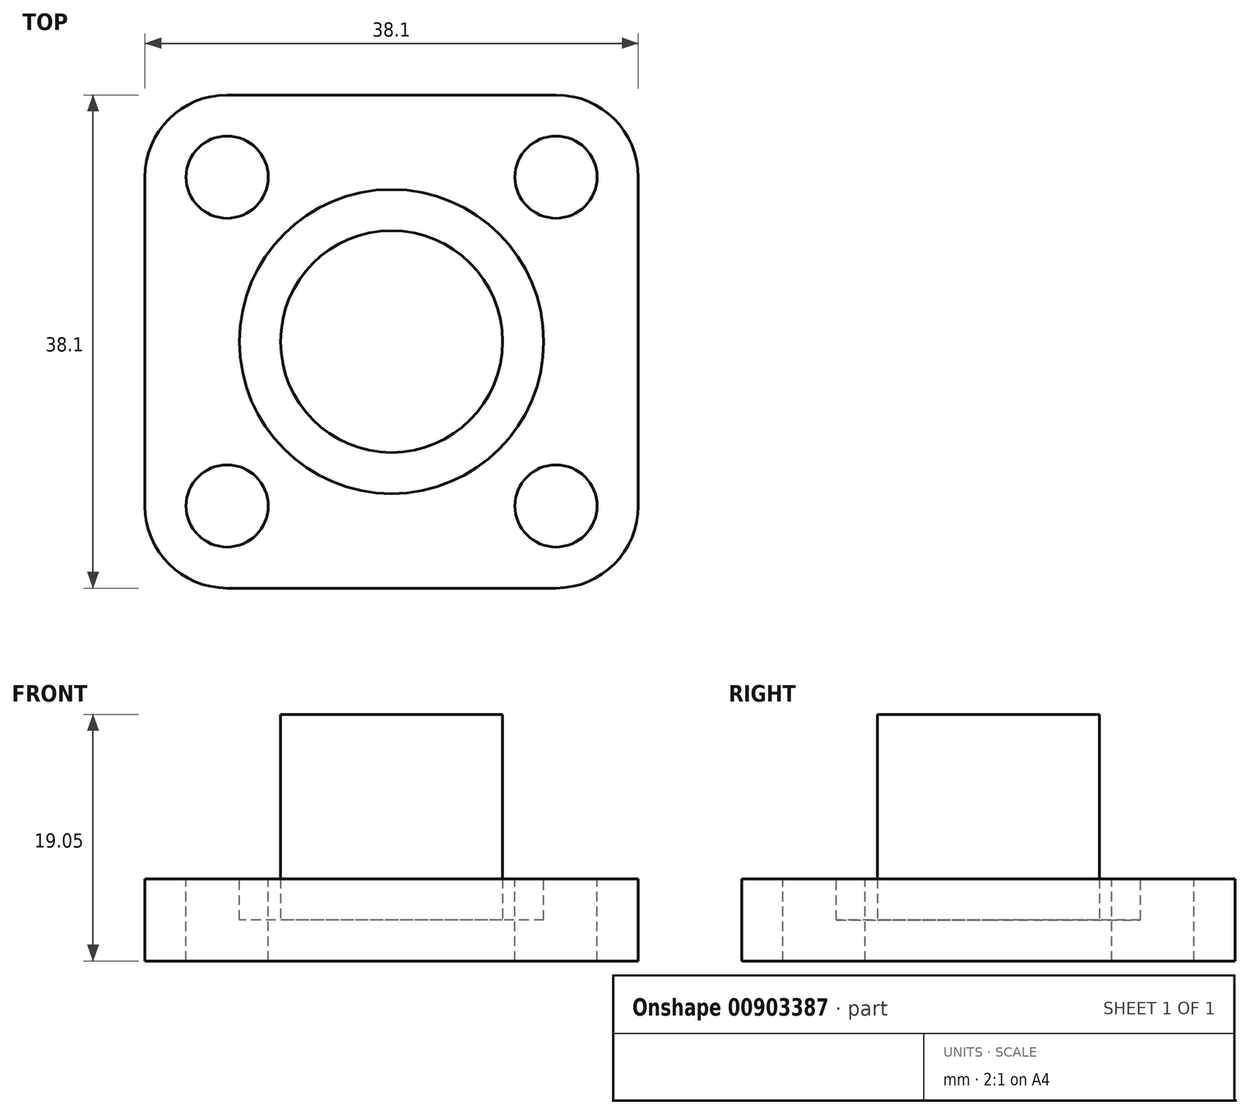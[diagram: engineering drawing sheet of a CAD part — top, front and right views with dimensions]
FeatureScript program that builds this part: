
annotation { "Feature Type Name" : "Feature", "Feature Type Description" : "" }
export const myFeature = defineFeature(function(context is Context, id is Id, definition is map)
    precondition{}
    {
        {
            var Q0;
            Q0=qCreatedBy(makeId("Top.planeOp"),FACE);
            var sketch = newSketch(context, id + "F0", { "sketchPlane" : qUnion([Q0])});
            skLineSegment(sketch, "E0.bottom", {"start": v(19.05, -19.05) * mm, "end": v(-19.05, -19.05) * mm});
            skLineSegment(sketch, "E0.top", {"start": v(19.05, 19.05) * mm, "end": v(-19.05, 19.05) * mm});
            skLineSegment(sketch, "E0.left", {"start": v(19.05, -19.05) * mm, "end": v(19.05, 19.05) * mm});
            skLineSegment(sketch, "E0.right", {"start": v(-19.05, -19.05) * mm, "end": v(-19.05, 19.05) * mm});
            skPoint(sketch, "E0.middle", {"position": v(0, 0) * mm});
            skSolve(sketch);
        }
        {
            var Q0;
            Q0=makeQuery(id+"F0.imprint","IMPRINT",FACE,{"disambiguationData":[TD([[makeQuery(id+"F0.imprint","IMPRINT",EDGE,{"derivedFrom":sQuery(id+"F0.wireOp",EDGE,"E0.bottom")}),-1.0]])]});
            extrude(context, id + "F1", {"entities" : qUnion([Q0]), "depth" : 6.35 * mm, "offsetDistance" : 25.4 * mm});
        }
        {
            var Q0;
            Q0=makeQuery(id+"F1.opExtrude","CAP_FACE",FACE,{"disambiguationData":[OSD([sQuery(id+"F0.wireOp",EDGE,"E0.bottom"),sQuery(id+"F0.wireOp",EDGE,"E0.top"),sQuery(id+"F0.wireOp",EDGE,"E0.left"),sQuery(id+"F0.wireOp",EDGE,"E0.right")])],"isStart":false});
            var sketch = newSketch(context, id + "F2", { "sketchPlane" : qUnion([Q0])});
            skLineSegment(sketch, "E1.bottom", {"start": v(12.7, -12.7) * mm, "end": v(-12.7, -12.7) * mm, "construction": true});
            skLineSegment(sketch, "E1.top", {"start": v(12.7, 12.7) * mm, "end": v(-12.7, 12.7) * mm, "construction": true});
            skLineSegment(sketch, "E1.left", {"start": v(12.7, -12.7) * mm, "end": v(12.7, 12.7) * mm, "construction": true});
            skLineSegment(sketch, "E1.right", {"start": v(-12.7, -12.7) * mm, "end": v(-12.7, 12.7) * mm, "construction": true});
            skPoint(sketch, "E1.middle", {"position": v(0, 0) * mm});
            skSolve(sketch);
        }
        {
            var Q0;
            Q0=sQuery(id+"F2.wireOp",VERTEX,"E1.top.end");
            var Q1;
            Q1=sQuery(id+"F2.wireOp",VERTEX,"E1.bottom.end");
            var Q2;
            Q2=sQuery(id+"F2.wireOp",VERTEX,"E1.bottom.start");
            var Q3;
            Q3=sQuery(id+"F2.wireOp",VERTEX,"E1.top.start");
            var Q4;
            Q4=makeQuery(id+"F1.opExtrude","SWEPT_BODY",BODY,{"disambiguationData":[OSD([sQuery(id+"F0.wireOp",EDGE,"E0.bottom"),sQuery(id+"F0.wireOp",EDGE,"E0.top"),sQuery(id+"F0.wireOp",EDGE,"E0.left"),sQuery(id+"F0.wireOp",EDGE,"E0.right")])]});
            hole(context, id + "F3", {"style" : HoleStyle.SIMPLE, "endStyle" : HoleEndStyle.THROUGH, "holeDiameter" : 6.35 * mm, "majorDiameter" : 6.35 * mm, "isTappedThrough" : true, "tappedDepth" : 12.7 * mm, "tapClearance" : 3, "locations" : qUnion([Q0, Q1, Q2, Q3]), "scope" : qUnion([Q4])});
        }
        {
            var Q0;
            Q0=makeQuery(id+"F1.opExtrude","SWEPT_EDGE",EDGE,{"disambiguationData":[OSD([sQuery(id+"F0.wireOp",EDGE,"E0.bottom"),sQuery(id+"F0.wireOp",EDGE,"E0.right")])]});
            var Q1;
            Q1=makeQuery(id+"F1.opExtrude","SWEPT_EDGE",EDGE,{"disambiguationData":[OSD([sQuery(id+"F0.wireOp",EDGE,"E0.bottom"),sQuery(id+"F0.wireOp",EDGE,"E0.left")])]});
            var Q2;
            Q2=makeQuery(id+"F1.opExtrude","SWEPT_EDGE",EDGE,{"disambiguationData":[OSD([sQuery(id+"F0.wireOp",EDGE,"E0.top"),sQuery(id+"F0.wireOp",EDGE,"E0.left")])]});
            var Q3;
            Q3=makeQuery(id+"F1.opExtrude","SWEPT_EDGE",EDGE,{"disambiguationData":[OSD([sQuery(id+"F0.wireOp",EDGE,"E0.top"),sQuery(id+"F0.wireOp",EDGE,"E0.right")])]});
            fillet(context, id + "F4", {"entities" : qUnion([Q0, Q1, Q2, Q3]), "radius" : 6.35 * mm, "tangentPropagation" : true, "allowEdgeOverflow" : false});
        }
        {
            var Q0;
            Q0=makeQuery(id+"F1.opExtrude","CAP_FACE",FACE,{"disambiguationData":[OSD([sQuery(id+"F0.wireOp",EDGE,"E0.bottom"),sQuery(id+"F0.wireOp",EDGE,"E0.top"),sQuery(id+"F0.wireOp",EDGE,"E0.left"),sQuery(id+"F0.wireOp",EDGE,"E0.right")])],"isStart":false});
            var sketch = newSketch(context, id + "F5", { "sketchPlane" : qUnion([Q0])});
            skCircle(sketch, "E2", {"center": v(0, 0) * mm, "radius": 8.57 * mm});
            skSolve(sketch);
        }
        {
            var Q0;
            Q0 = qSketchRegion(id + "F5", true);
            extrude(context, id + "F6", {"entities" : qUnion([Q0]), "operationType" : NewBodyOperationType.ADD, "depth" : 12.7 * mm, "offsetDistance" : 25.4 * mm});
        }
        {
            var Q0;
            Q0=makeQuery(id+"F1.opExtrude","CAP_FACE",FACE,{"disambiguationData":[OSD([sQuery(id+"F0.wireOp",EDGE,"E0.bottom"),sQuery(id+"F0.wireOp",EDGE,"E0.top"),sQuery(id+"F0.wireOp",EDGE,"E0.left"),sQuery(id+"F0.wireOp",EDGE,"E0.right")])],"isStart":false});
            var sketch = newSketch(context, id + "F7", { "sketchPlane" : qUnion([Q0])});
            skCircle(sketch, "E3", {"center": v(0, 0) * mm, "radius": 11.75 * mm});
            skCircle(sketch, "E4", {"center": v(0, 0) * mm, "radius": 8.57 * mm});
            skSolve(sketch);
        }
        {
            var Q0;
            Q0 = qSketchRegion(id + "F7", true);
            extrude(context, id + "F8", {"entities" : qUnion([Q0]), "operationType" : NewBodyOperationType.REMOVE, "oppositeDirection" : true, "depth" : 3.17 * mm, "offsetDistance" : 25.4 * mm});
        }
    });
